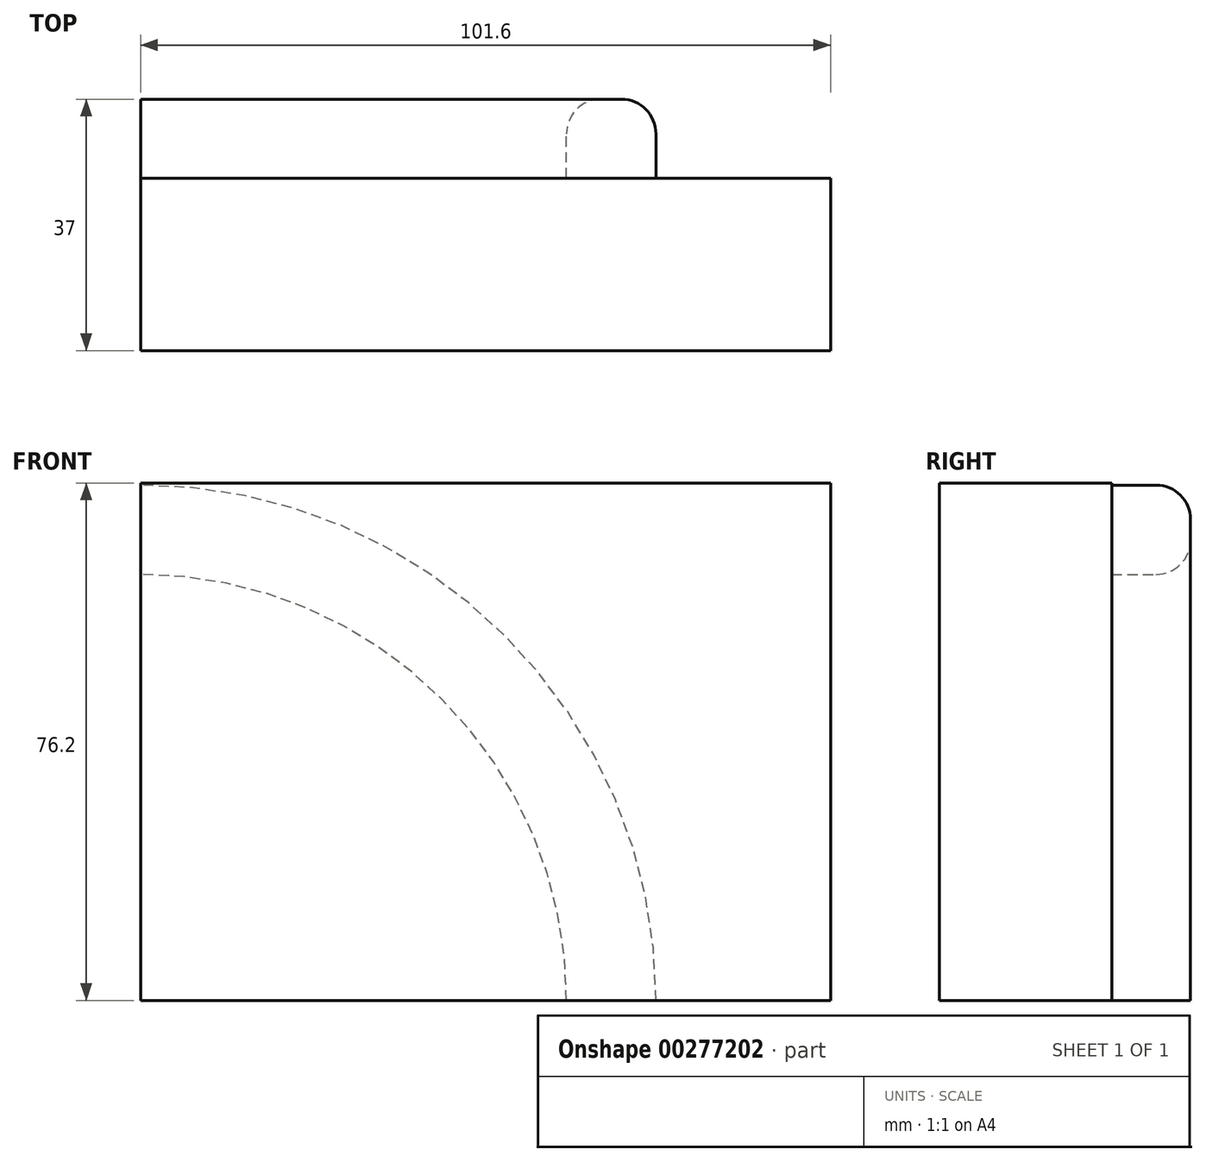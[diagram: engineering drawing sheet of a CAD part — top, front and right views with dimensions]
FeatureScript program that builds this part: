
annotation { "Feature Type Name" : "Feature", "Feature Type Description" : "" }
export const myFeature = defineFeature(function(context is Context, id is Id, definition is map)
    precondition{}
    {
        {
            var Q0;
            Q0=qCreatedBy(makeId("Front.planeOp"),FACE);
            var sketch = newSketch(context, id + "F0", { "sketchPlane" : qUnion([Q0])});
            skLineSegment(sketch, "E0.bottom", {"start": v(0, 0) * mm, "end": v(101.6, 0) * mm});
            skLineSegment(sketch, "E0.top", {"start": v(0, 76.2) * mm, "end": v(101.6, 76.2) * mm});
            skLineSegment(sketch, "E0.left", {"start": v(0, 0) * mm, "end": v(0, 76.2) * mm});
            skLineSegment(sketch, "E0.right", {"start": v(101.6, 0) * mm, "end": v(101.6, 76.2) * mm});
            skArc(sketch, "E1", {"start": v(76.2, 0) * mm, "mid": v(53.88, 53.88) * mm, "end": v(0, 76.2) * mm});
            skSolve(sketch);
        }
        {
            var Q0;
            Q0=makeQuery(id+"F0.imprint","IMPRINT",FACE,{"disambiguationData":[TD([[makeQuery(id+"F0.imprint","IMPRINT",EDGE,{"derivedFrom":sQuery(id+"F0.wireOp",EDGE,"E0.bottom")}),1.0]])]});
            extrude(context, id + "F1", {"entities" : qUnion([Q0]), "depth" : 12.7 * mm});
        }
        {
            var Q0;
            Q0=qCreatedBy(makeId("Top.planeOp"),FACE);
            var sketch = newSketch(context, id + "F2", { "sketchPlane" : qUnion([Q0])});
            skLineSegment(sketch, "E2.bottom", {"start": v(75.89, 0) * mm, "end": v(62.72, 0) * mm});
            skLineSegment(sketch, "E2.top", {"start": v(75.89, 11.6) * mm, "end": v(62.72, 11.6) * mm});
            skLineSegment(sketch, "E2.left", {"start": v(75.89, 0) * mm, "end": v(75.89, 11.6) * mm});
            skLineSegment(sketch, "E2.right", {"start": v(62.72, 0) * mm, "end": v(62.72, 11.6) * mm});
            skSolve(sketch);
        }
        {
            var Q0;
            Q0=makeQuery(id+"F2.imprint","IMPRINT",FACE,{"disambiguationData":[TD([[makeQuery(id+"F2.imprint","IMPRINT",EDGE,{"derivedFrom":sQuery(id+"F2.wireOp",EDGE,"E2.bottom")}),-1.0]])]});
            var Q1;
            Q1=sQuery(id+"F0.wireOp",EDGE,"E1");
            sweep(context, id + "F3", {"profiles" : qUnion([Q0]), "path" : qUnion([Q1])});
        }
        {
            var Q0;
            Q0=makeQuery(id+"F0.imprint","IMPRINT",FACE,{"disambiguationData":[TD([[makeQuery(id+"F0.imprint","IMPRINT",EDGE,{"derivedFrom":sQuery(id+"F0.wireOp",EDGE,"E0.top")}),-1.0]])]});
            extrude(context, id + "F4", {"entities" : qUnion([Q0]), "operationType" : NewBodyOperationType.ADD, "depth" : 25.4 * mm});
        }
        {
            var Q0;
            Q0=makeQuery(id+"F1.opExtrude","CAP_FACE",FACE,{"disambiguationData":[OSD([sQuery(id+"F0.wireOp",EDGE,"E0.bottom"),sQuery(id+"F0.wireOp",EDGE,"E0.left"),sQuery(id+"F0.wireOp",EDGE,"E1")])],"isStart":false});
            extrude(context, id + "F5", {"entities" : qUnion([Q0]), "operationType" : NewBodyOperationType.ADD, "depth" : 12.7 * mm});
        }
        {
            var Q0;
            Q0=makeQuery(id+"F3.opSweep","SWEPT_EDGE",EDGE,{"disambiguationData":[OSD([sQuery(id+"F0.wireOp",EDGE,"E1"),sQuery(id+"F2.wireOp",EDGE,"E2.top"),sQuery(id+"F2.wireOp",EDGE,"E2.left")])]});
            var Q1;
            Q1=makeQuery(id+"F3.opSweep","SWEPT_EDGE",EDGE,{"disambiguationData":[OSD([sQuery(id+"F0.wireOp",EDGE,"E1"),sQuery(id+"F2.wireOp",EDGE,"E2.top"),sQuery(id+"F2.wireOp",EDGE,"E2.right")])]});
            fillet(context, id + "F6", {"entities" : qUnion([Q0, Q1]), "radius" : 5.08 * mm, "tangentPropagation" : true, "allowEdgeOverflow" : false});
        }
    });
